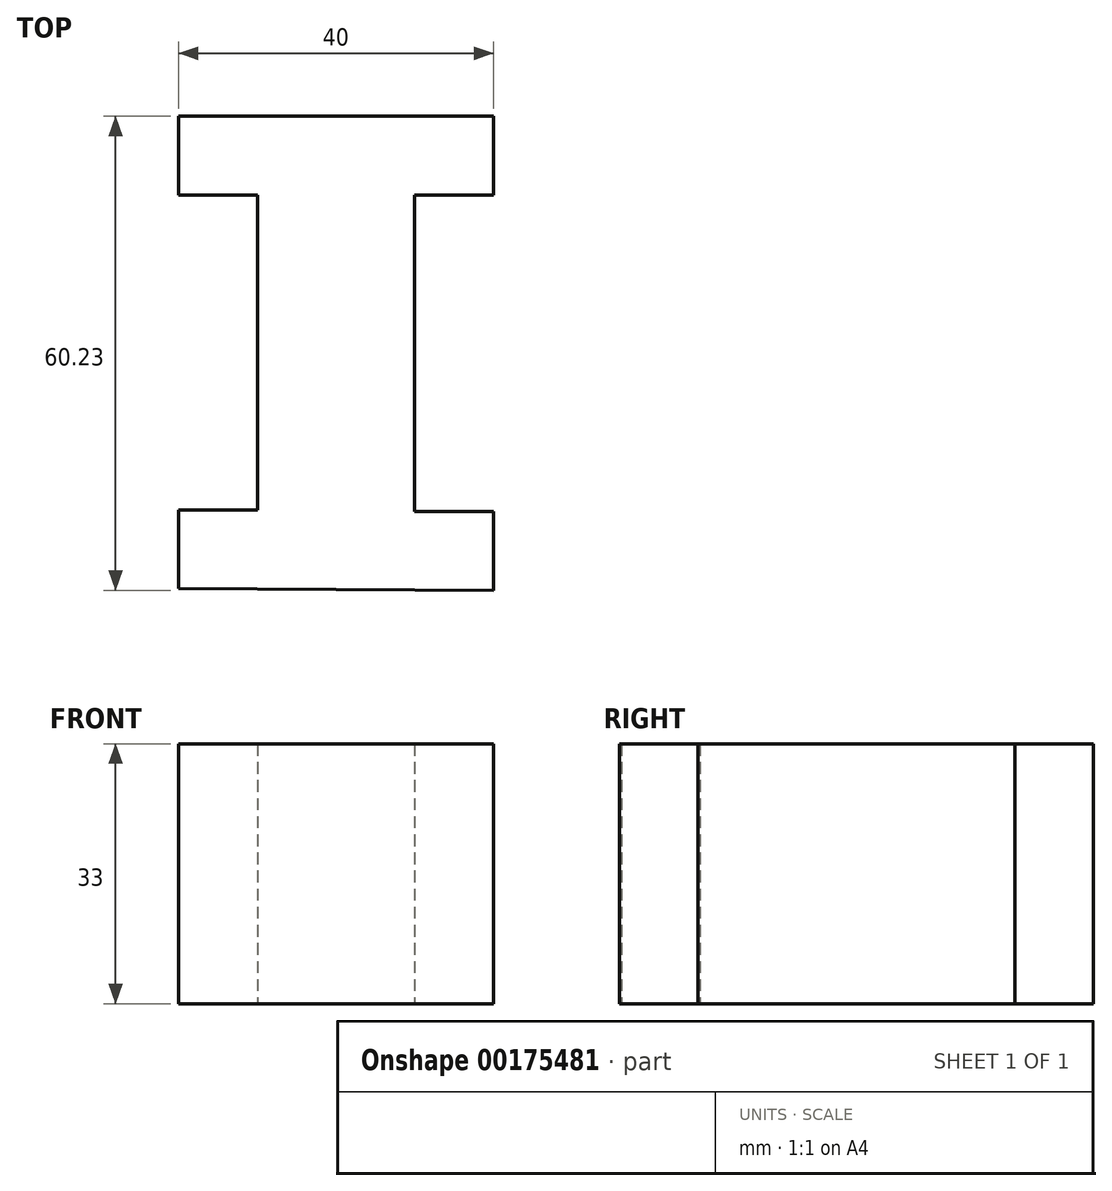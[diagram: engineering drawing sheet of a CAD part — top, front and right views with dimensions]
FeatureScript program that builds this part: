
annotation { "Feature Type Name" : "Feature", "Feature Type Description" : "" }
export const myFeature = defineFeature(function(context is Context, id is Id, definition is map)
    precondition{}
    {
        {
            var Q0;
            Q0=qCreatedBy(makeId("Top.planeOp"),FACE);
            var sketch = newSketch(context, id + "F0", { "sketchPlane" : qUnion([Q0])});
            skLineSegment(sketch, "E0", {"start": v(-53.6, 37.2) * mm, "end": v(-13.6, 37.2) * mm});
            skLineSegment(sketch, "E1", {"start": v(-53.6, 37.2) * mm, "end": v(-53.6, 27.2) * mm});
            skLineSegment(sketch, "E2", {"start": v(-13.6, 37.2) * mm, "end": v(-13.6, 27.2) * mm});
            skLineSegment(sketch, "E3", {"start": v(-53.6, 27.2) * mm, "end": v(-43.6, 27.2) * mm});
            skLineSegment(sketch, "E4", {"start": v(-13.6, 27.2) * mm, "end": v(-23.6, 27.2) * mm});
            skLineSegment(sketch, "E5", {"start": v(-43.6, 27.2) * mm, "end": v(-43.6, -12.8) * mm});
            skLineSegment(sketch, "E6", {"start": v(-23.6, 27.2) * mm, "end": v(-23.6, -13.04) * mm});
            skLineSegment(sketch, "E7", {"start": v(-23.6, -13.04) * mm, "end": v(-13.6, -13.04) * mm});
            skLineSegment(sketch, "E8", {"start": v(-43.6, -12.8) * mm, "end": v(-53.6, -12.8) * mm});
            skLineSegment(sketch, "E9", {"start": v(-53.6, -12.8) * mm, "end": v(-53.6, -22.8) * mm});
            skLineSegment(sketch, "E10", {"start": v(-13.6, -13.04) * mm, "end": v(-13.6, -23.04) * mm});
            skLineSegment(sketch, "E11", {"start": v(-53.6, -22.8) * mm, "end": v(-13.6, -23.04) * mm});
            skSolve(sketch);
        }
        {
            var Q0;
            Q0=makeQuery(id+"F0.imprint","IMPRINT",FACE,{"disambiguationData":[TD([[makeQuery(id+"F0.imprint","IMPRINT",EDGE,{"derivedFrom":sQuery(id+"F0.wireOp",EDGE,"E0")}),-1.0]])]});
            extrude(context, id + "F1", {"entities" : qUnion([Q0]), "depth" : 33 * mm});
        }
    });
